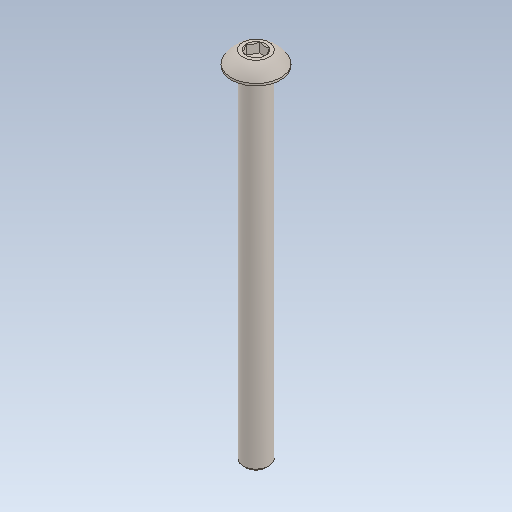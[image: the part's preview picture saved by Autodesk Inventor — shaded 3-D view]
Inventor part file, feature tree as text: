
AUTODESK INVENTOR PART (.ipt)
format: ipt  version: 2020 (Build 240168000, 168)  size: 106,496 bytes
history: native  units: in
note: dims shown in document units (in); Inventor stores cm internally (conversion verified against a paired STEP export)
features: fillet x1
ambient origin geometry x8: Origin, YZ Plane, XZ Plane, XY Plane, X Axis, Y Axis, Z Axis, Center Point
bodies: Solid1 (feature_tree)
feature tree (1):
  fillet  "Fillet1"  [1 undecoded]
note: 1 required parameter value undecoded (feature->parameter linkage not recoverable at this tier; creation-order binding heuristic only, values carry confidence <= 0.55)
